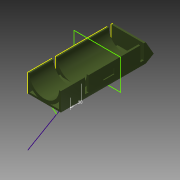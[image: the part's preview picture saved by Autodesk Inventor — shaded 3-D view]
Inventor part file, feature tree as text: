
AUTODESK INVENTOR PART (.ipt)
format: ipt  version: 2013 (Build 170138000, 138)  size: 249,856 bytes
history: native  units: mm
features: sketch x12, extrude x9, other x1, hole x1
ambient origin geometry x8: Origin, YZ Plane, XZ Plane, XY Plane, X Axis, Y Axis, Z Axis, Center Point
feature tree (23):
  other  "ソリッド1"
  extrude  "押し出し1"  Depth=90.0mm
  extrude  "押し出し2"  Depth=50.0mm
  extrude  "押し出し3"  Depth=5.0mm
  extrude  "押し出し4"  Depth=85.0mm
  extrude  "押し出し6"  Depth=5.0mm
  sketch  "スケッチ9"
  hole  "穴1"  [1 undecoded]
  extrude  "押し出し8"  Depth=10.0mm
  extrude  "押し出し9"  Depth=90.0mm
  extrude  "押し出し10"  Depth=230.0mm TaperAngle=0.0deg
  extrude  "押し出し11"  Depth=225.0mm TaperAngle=0.0deg
  sketch  "スケッチ17"
  sketch  "スケッチ1"
  sketch  "スケッチ2"
  sketch  "スケッチ3"
  sketch  "スケッチ4"
  sketch  "スケッチ6"
  sketch  "スケッチ11"
  sketch  "スケッチ12"
  sketch  "スケッチ13"
  sketch  "スケッチ14"
  sketch  "スケッチ16"
note: 1 required parameter value undecoded (feature->parameter linkage not recoverable at this tier; creation-order binding heuristic only, values carry confidence <= 0.55)
